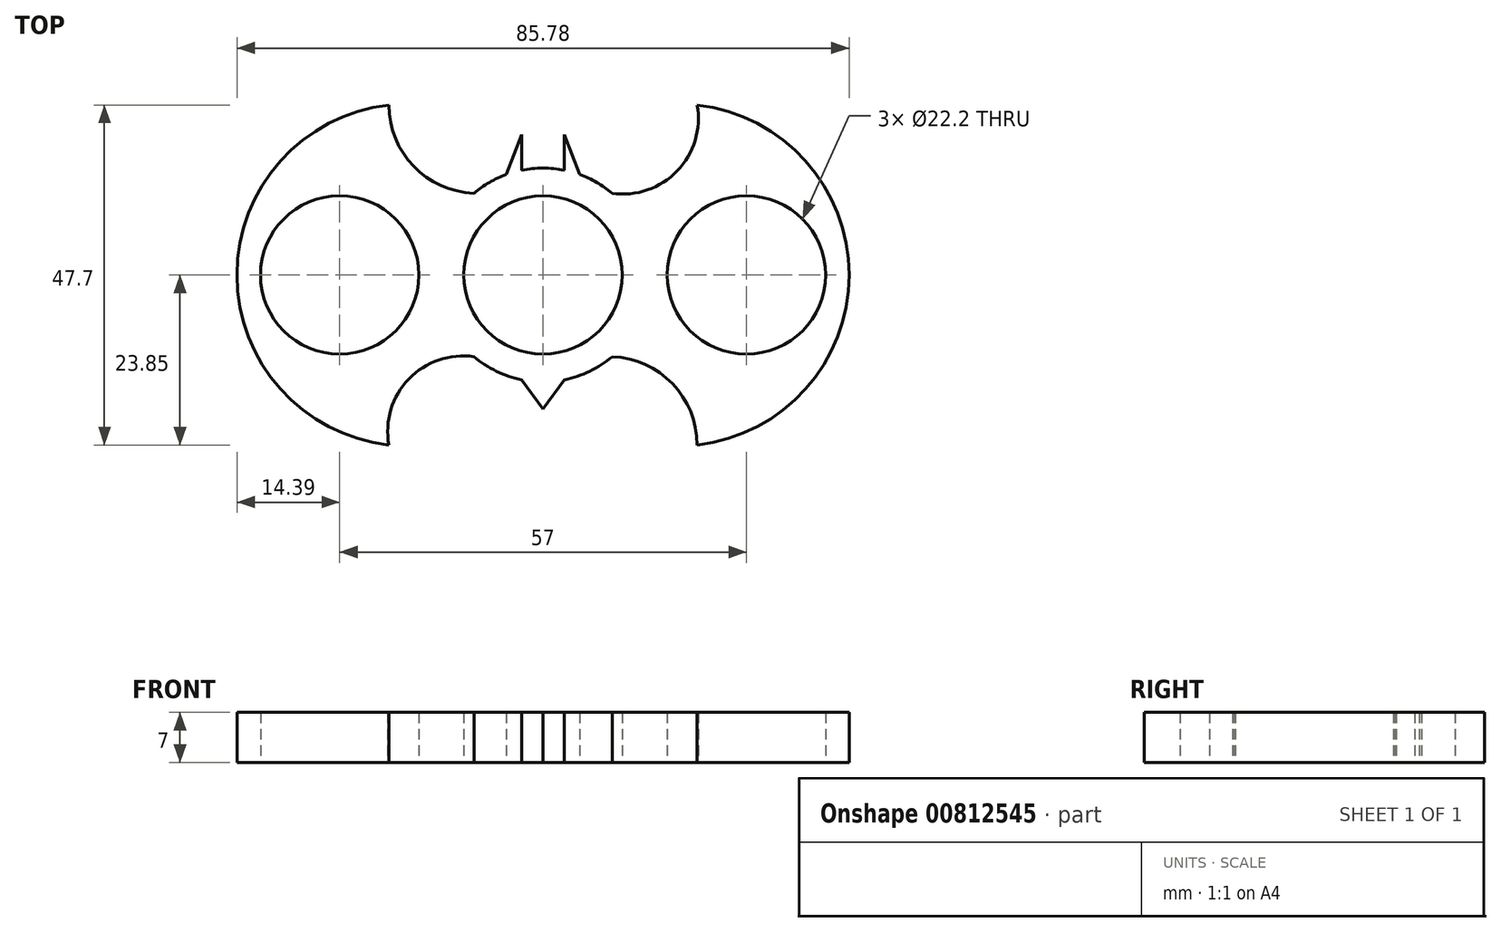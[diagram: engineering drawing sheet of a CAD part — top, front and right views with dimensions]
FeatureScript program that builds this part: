
annotation { "Feature Type Name" : "Feature", "Feature Type Description" : "" }
export const myFeature = defineFeature(function(context is Context, id is Id, definition is map)
    precondition{}
    {
        {
            var Q0;
            Q0=qCreatedBy(makeId("Top.planeOp"),FACE);
            var sketch = newSketch(context, id + "F0", { "sketchPlane" : qUnion([Q0])});
            skCircle(sketch, "E0", {"center": v(0, 0) * mm, "radius": 11.1 * mm});
            skArc(sketch, "E1", {"start": v(9.68, 11.46) * mm, "mid": v(7.52, 12.98) * mm, "end": v(5.14, 14.1) * mm});
            skArc(sketch, "E2", {"start": v(21.6, -23.85) * mm, "mid": v(42.89, 0) * mm, "end": v(21.6, 23.85) * mm});
            skArc(sketch, "E3", {"start": v(9.68, 11.46) * mm, "mid": v(18.81, 14.6) * mm, "end": v(21.6, 23.85) * mm});
            skArc(sketch, "E4", {"start": v(21.6, -23.85) * mm, "mid": v(18.13, -15.25) * mm, "end": v(9.68, -11.46) * mm});
            skPoint(sketch, "E5.end.orphan", {"position": v(9.68, 0) * mm});
            skArc(sketch, "E6.1.0", {"start": v(-9.68, -11.46) * mm, "mid": v(-18.81, -14.6) * mm, "end": v(-21.6, -23.85) * mm});
            skArc(sketch, "E6.1.1", {"start": v(-21.6, 23.85) * mm, "mid": v(-42.89, 0) * mm, "end": v(-21.6, -23.85) * mm});
            skArc(sketch, "E6.1.2", {"start": v(-21.6, 23.85) * mm, "mid": v(-18.13, 15.25) * mm, "end": v(-9.68, 11.46) * mm});
            skLineSegment(sketch, "E7", {"start": v(3, 14.7) * mm, "end": v(3, 17.7) * mm});
            skLineSegment(sketch, "E8", {"start": v(-3, 14.7) * mm, "end": v(-3, 17.7) * mm});
            skPoint(sketch, "E9.end.orphan", {"position": v(3, 15) * mm});
            skPoint(sketch, "E9.start.orphan", {"position": v(0, 15) * mm});
            skLineSegment(sketch, "E10", {"start": v(3, 15) * mm, "end": v(3, 14.7) * mm});
            skLineSegment(sketch, "E11", {"start": v(3, -14.7) * mm, "end": v(0, -18.8) * mm});
            skLineSegment(sketch, "E12", {"start": v(0, -18.8) * mm, "end": v(-3, -14.7) * mm});
            skLineSegment(sketch, "E13", {"start": v(3, 14.7) * mm, "end": v(3, 19.7) * mm});
            skLineSegment(sketch, "E14", {"start": v(3, 19.7) * mm, "end": v(5.14, 14.1) * mm});
            skLineSegment(sketch, "E15", {"start": v(-3, 14.7) * mm, "end": v(-3, 19.7) * mm});
            skPoint(sketch, "E15.endSnap0", {"position": v(-3, 16.2) * mm});
            skLineSegment(sketch, "E16", {"start": v(-3, 19.7) * mm, "end": v(-5.14, 14.1) * mm});
            skArc(sketch, "E17.trimOffspring", {"start": v(-9.68, -11.46) * mm, "mid": v(-6.54, -13.5) * mm, "end": v(-3, -14.7) * mm});
            skArc(sketch, "E18.trimOffspring", {"start": v(-5.14, 14.1) * mm, "mid": v(-7.52, 12.98) * mm, "end": v(-9.68, 11.46) * mm});
            skArc(sketch, "E19.trimOffspring", {"start": v(3, 14.7) * mm, "mid": v(0, 15) * mm, "end": v(-3, 14.7) * mm});
            skArc(sketch, "E20.trimOffspring", {"start": v(3, -14.7) * mm, "mid": v(6.54, -13.5) * mm, "end": v(9.68, -11.46) * mm});
            skCircle(sketch, "E21", {"center": v(-28.5, 0) * mm, "radius": 11.1 * mm});
            skCircle(sketch, "E22", {"center": v(28.5, 0) * mm, "radius": 11.1 * mm});
            skSolve(sketch);
        }
        {
            var Q0;
            Q0 = qSketchRegion(id + "F0", true);
            extrude(context, id + "F1", {"entities" : qUnion([Q0]), "depth" : 7 * mm, "offsetDistance" : 25 * mm});
        }
    });
